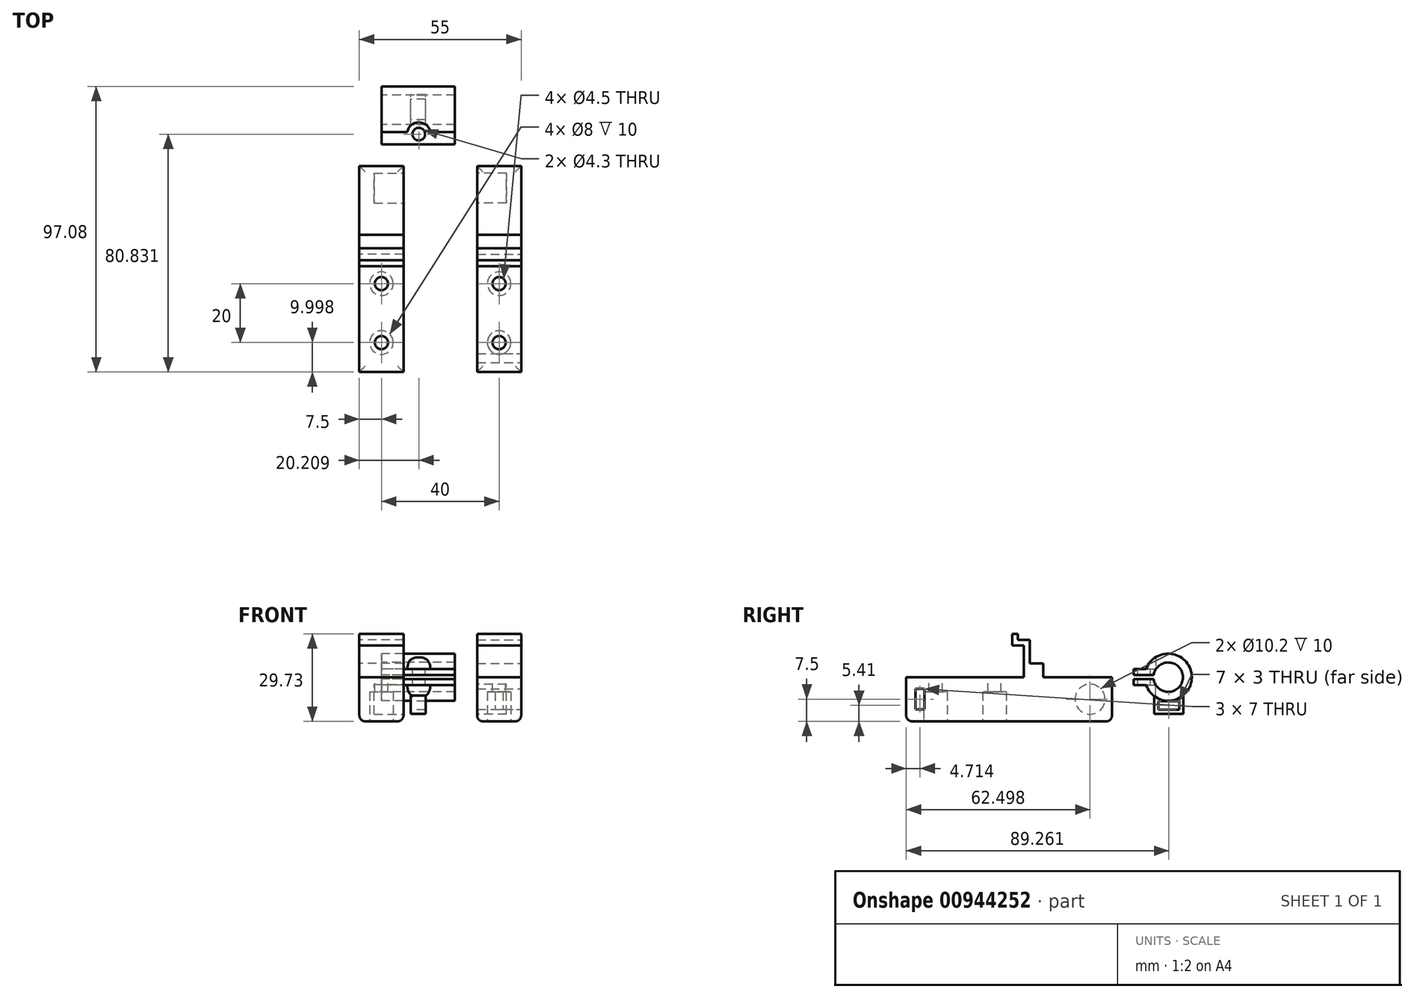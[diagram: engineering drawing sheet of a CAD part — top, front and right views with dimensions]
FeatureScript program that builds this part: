
annotation { "Feature Type Name" : "Feature", "Feature Type Description" : "" }
export const myFeature = defineFeature(function(context is Context, id is Id, definition is map)
    precondition{}
    {
        {
            var Q0;
            Q0=qCreatedBy(makeId("Top.planeOp"),FACE);
            var sketch = newSketch(context, id + "F0", { "sketchPlane" : qUnion([Q0])});
            skLineSegment(sketch, "E0", {"start": v(120.64, 20) * mm, "end": v(-98.83, 20) * mm, "construction": true});
            skLineSegment(sketch, "E1", {"start": v(-113.57, -20) * mm, "end": v(119.85, -20) * mm, "construction": true});
            skLineSegment(sketch, "E2", {"start": v(-15.81, 35.6) * mm, "end": v(120.22, 35.6) * mm, "construction": true});
            skLineSegment(sketch, "E3", {"start": v(0, 0) * mm, "end": v(121.2, 0) * mm, "construction": true});
            skSolve(sketch);
        }
        {
            var Q0;
            Q0=qCreatedBy(makeId("Right.planeOp"),FACE);
            var sketch = newSketch(context, id + "F1", { "sketchPlane" : qUnion([Q0])});
            skLineSegment(sketch, "E4", {"start": v(13.49, 0) * mm, "end": v(-26.51, 0) * mm});
            skLineSegment(sketch, "E5", {"start": v(-26.51, 0) * mm, "end": v(-26.51, -15) * mm});
            skLineSegment(sketch, "E6", {"start": v(-26.51, -15) * mm, "end": v(18.49, -15) * mm});
            skLineSegment(sketch, "E7", {"start": v(13.49, 10.73) * mm, "end": v(13.49, 0) * mm});
            skLineSegment(sketch, "E8", {"start": v(43.49, -15) * mm, "end": v(43.49, 0) * mm});
            skLineSegment(sketch, "E9", {"start": v(43.49, 0) * mm, "end": v(20.14, 0) * mm});
            skLineSegment(sketch, "E10", {"start": v(13.49, 10.73) * mm, "end": v(9.49, 10.73) * mm});
            skLineSegment(sketch, "E11", {"start": v(9.49, 10.73) * mm, "end": v(9.49, 14.73) * mm});
            skLineSegment(sketch, "E12", {"start": v(9.49, 14.73) * mm, "end": v(11.49, 14.73) * mm});
            skLineSegment(sketch, "E13", {"start": v(11.49, 14.73) * mm, "end": v(11.49, 12.73) * mm});
            skLineSegment(sketch, "E14", {"start": v(18.49, -15) * mm, "end": v(43.49, -15) * mm});
            skLineSegment(sketch, "E15", {"start": v(20.14, 0) * mm, "end": v(20.14, 4.7) * mm});
            skLineSegment(sketch, "E16", {"start": v(20.14, 4.7) * mm, "end": v(15.49, 4.7) * mm});
            skPoint(sketch, "E17.orphan", {"position": v(15.49, 0) * mm});
            skPoint(sketch, "E18.end.orphan", {"position": v(13.49, 21.47) * mm});
            skLineSegment(sketch, "E19", {"start": v(15.49, 4.7) * mm, "end": v(15.49, 12.7) * mm});
            skPoint(sketch, "E20.end.orphan", {"position": v(13.49, 12) * mm});
            skLineSegment(sketch, "E21", {"start": v(15.49, 12.7) * mm, "end": v(11.49, 12.73) * mm});
            skSolve(sketch);
        }
        {
            var Q0;
            Q0=makeQuery(id+"F1.imprint","IMPRINT",FACE,{"disambiguationData":[TD([[makeQuery(id+"F1.imprint","IMPRINT",EDGE,{"derivedFrom":sQuery(id+"F1.wireOp",EDGE,"E4")}),1.0]])]});
            var Q1;
            {var subQ0=sQuery(id+"F1.wireOp",EDGE,"E10");Q1=makeQuery(id+"F1.imprint","IMPRINT",FACE,{"disambiguationData":[TD([[makeQuery(id+"F1.imprint","IMPRINT",EDGE,{"derivedFrom":subQ0}),-1.0]])]});}
            extrude(context, id + "F2", {"entities" : qUnion([Q0, Q1]), "depth" : 15 * mm, "symmetric" : true});
        }
        {
            var Q0;
            Q0=makeQuery(id+"F2.opExtrude","CAP_FACE",FACE,{"disambiguationData":[OSD([sQuery(id+"F1.wireOp",EDGE,"E4"),sQuery(id+"F1.wireOp",EDGE,"E5"),sQuery(id+"F1.wireOp",EDGE,"E6"),sQuery(id+"F1.wireOp",EDGE,"E7"),sQuery(id+"F1.wireOp",EDGE,"E8"),sQuery(id+"F1.wireOp",EDGE,"E9"),sQuery(id+"F1.wireOp",EDGE,"E10"),sQuery(id+"F1.wireOp",EDGE,"E11"),sQuery(id+"F1.wireOp",EDGE,"E12"),sQuery(id+"F1.wireOp",EDGE,"E13"),sQuery(id+"F1.wireOp",EDGE,"E14"),sQuery(id+"F1.wireOp",EDGE,"E15"),sQuery(id+"F1.wireOp",EDGE,"E16"),sQuery(id+"F1.wireOp",EDGE,"E19"),sQuery(id+"F1.wireOp",EDGE,"E21")])],"isStart":false});
            var sketch = newSketch(context, id + "F3", { "sketchPlane" : qUnion([Q0])});
            skCircle(sketch, "E22", {"center": v(35.99, -7.5) * mm, "radius": 5.1 * mm});
            skSolve(sketch);
        }
        {
            var Q0;
            Q0=makeQuery(id+"F3.imprint","IMPRINT",FACE,{"disambiguationData":[TD([[makeQuery(id+"F3.imprint","IMPRINT",EDGE,{"derivedFrom":sQuery(id+"F3.wireOp",EDGE,"E22")}),1.0]])]});
            extrude(context, id + "F4", {"entities" : qUnion([Q0]), "operationType" : NewBodyOperationType.REMOVE, "oppositeDirection" : true, "depth" : 10 * mm});
        }
        {
            var Q0;
            Q0=qCreatedBy(makeId("Right.planeOp"),FACE);
            cPlane(context, id + "F5", {"entities" : qUnion([Q0]), "cplaneType" : CPlaneType.OFFSET, "offset" : 20 * mm, "width" : 150 * mm, "height" : 150 * mm});
        }
        {
            var Q0;
            Q0=makeQuery(id+"F2.opExtrude","SWEPT_BODY",BODY,{"disambiguationData":[OSD([sQuery(id+"F1.wireOp",EDGE,"E4"),sQuery(id+"F1.wireOp",EDGE,"E5"),sQuery(id+"F1.wireOp",EDGE,"E6"),sQuery(id+"F1.wireOp",EDGE,"E7"),sQuery(id+"F1.wireOp",EDGE,"E8"),sQuery(id+"F1.wireOp",EDGE,"E9"),sQuery(id+"F1.wireOp",EDGE,"E10"),sQuery(id+"F1.wireOp",EDGE,"E11"),sQuery(id+"F1.wireOp",EDGE,"E12"),sQuery(id+"F1.wireOp",EDGE,"E13"),sQuery(id+"F1.wireOp",EDGE,"E14"),sQuery(id+"F1.wireOp",EDGE,"E15"),sQuery(id+"F1.wireOp",EDGE,"E16"),sQuery(id+"F1.wireOp",EDGE,"E19"),sQuery(id+"F1.wireOp",EDGE,"E21")])]});
            var Q1;
            Q1=qCreatedBy(id+"F5.planeOp",FACE);
            mirror(context, id + "F6", {"entities" : qUnion([Q0]), "mirrorPlane" : qUnion([Q1])});
        }
        {
            var Q0;
            Q0=makeQuery(id+"F6.opPattern","COPY",FACE,{"derivedFrom":makeQuery(id+"F2.opExtrude","CAP_FACE",FACE,{"disambiguationData":[OSD([sQuery(id+"F1.wireOp",EDGE,"E4"),sQuery(id+"F1.wireOp",EDGE,"E5"),sQuery(id+"F1.wireOp",EDGE,"E6"),sQuery(id+"F1.wireOp",EDGE,"E7"),sQuery(id+"F1.wireOp",EDGE,"E8"),sQuery(id+"F1.wireOp",EDGE,"E9"),sQuery(id+"F1.wireOp",EDGE,"E10"),sQuery(id+"F1.wireOp",EDGE,"E11"),sQuery(id+"F1.wireOp",EDGE,"E12"),sQuery(id+"F1.wireOp",EDGE,"E13"),sQuery(id+"F1.wireOp",EDGE,"E14"),sQuery(id+"F1.wireOp",EDGE,"E15"),sQuery(id+"F1.wireOp",EDGE,"E16"),sQuery(id+"F1.wireOp",EDGE,"E19"),sQuery(id+"F1.wireOp",EDGE,"E21")])],"isStart":true}),"instanceName":"1"});
            var sketch = newSketch(context, id + "F7", { "sketchPlane" : qUnion([Q0])});
            skLineSegment(sketch, "E23.bottom", {"start": v(-20.3, -4) * mm, "end": v(-23.3, -4) * mm});
            skLineSegment(sketch, "E23.top", {"start": v(-20.3, -11) * mm, "end": v(-23.3, -11) * mm});
            skLineSegment(sketch, "E23.left", {"start": v(-20.3, -4) * mm, "end": v(-20.3, -11) * mm});
            skLineSegment(sketch, "E23.right", {"start": v(-23.3, -4) * mm, "end": v(-23.3, -11) * mm});
            skSolve(sketch);
        }
        {
            var Q0;
            Q0=makeQuery(id+"F7.imprint","IMPRINT",FACE,{"disambiguationData":[TD([[makeQuery(id+"F7.imprint","IMPRINT",EDGE,{"derivedFrom":sQuery(id+"F7.wireOp",EDGE,"E23.bottom")}),1.0]])]});
            extrude(context, id + "F8", {"entities" : qUnion([Q0]), "operationType" : NewBodyOperationType.REMOVE, "endBound" : BoundingType.UP_TO_NEXT, "oppositeDirection" : true, "depth" : 25 * mm});
        }
        {
            var Q0;
            Q0=makeQuery(id+"F8.boolean.opBoolean","COPY",EDGE,{"derivedFrom":makeQuery(id+"F8.opExtrude","CAP_EDGE",EDGE,{"disambiguationData":[OSD([sQuery(id+"F7.wireOp",EDGE,"E23.right")])],"isStart":true})});
            var Q1;
            Q1=makeQuery(id+"F8.boolean.opBoolean","COPY",EDGE,{"derivedFrom":makeQuery(id+"F8.opExtrude","TWEAK_EDGE",EDGE,{"derivedFrom":[makeQuery(id+"F6.opPattern","COPY",FACE,{"derivedFrom":makeQuery(id+"F2.opExtrude","CAP_FACE",FACE,{"disambiguationData":[OSD([sQuery(id+"F1.wireOp",EDGE,"E4"),sQuery(id+"F1.wireOp",EDGE,"E5"),sQuery(id+"F1.wireOp",EDGE,"E6"),sQuery(id+"F1.wireOp",EDGE,"E7"),sQuery(id+"F1.wireOp",EDGE,"E8"),sQuery(id+"F1.wireOp",EDGE,"E9"),sQuery(id+"F1.wireOp",EDGE,"E10"),sQuery(id+"F1.wireOp",EDGE,"E11"),sQuery(id+"F1.wireOp",EDGE,"E12"),sQuery(id+"F1.wireOp",EDGE,"E13"),sQuery(id+"F1.wireOp",EDGE,"E14"),sQuery(id+"F1.wireOp",EDGE,"E15"),sQuery(id+"F1.wireOp",EDGE,"E16"),sQuery(id+"F1.wireOp",EDGE,"E19"),sQuery(id+"F1.wireOp",EDGE,"E21")])],"isStart":false}),"instanceName":"1"}),makeQuery(id+"F7.imprint","IMPRINT",EDGE,{"derivedFrom":sQuery(id+"F7.wireOp",EDGE,"E23.right")})]})});
            var Q2;
            Q2=makeQuery(id+"F6.opPattern","COPY",EDGE,{"derivedFrom":makeQuery(id+"F2.opExtrude","CAP_EDGE",EDGE,{"disambiguationData":[OSD([sQuery(id+"F1.wireOp",EDGE,"E6"),sQuery(id+"F1.wireOp",EDGE,"E14")])],"isStart":false}),"instanceName":"1"});
            var Q3;
            Q3=makeQuery(id+"F6.opPattern","COPY",EDGE,{"derivedFrom":makeQuery(id+"F2.opExtrude","CAP_EDGE",EDGE,{"disambiguationData":[OSD([sQuery(id+"F1.wireOp",EDGE,"E6"),sQuery(id+"F1.wireOp",EDGE,"E14")])],"isStart":true}),"instanceName":"1"});
            var Q4;
            Q4=makeQuery(id+"F2.opExtrude","CAP_EDGE",EDGE,{"disambiguationData":[OSD([sQuery(id+"F1.wireOp",EDGE,"E6"),sQuery(id+"F1.wireOp",EDGE,"E14")])],"isStart":true});
            var Q5;
            Q5=makeQuery(id+"F2.opExtrude","CAP_EDGE",EDGE,{"disambiguationData":[OSD([sQuery(id+"F1.wireOp",EDGE,"E6"),sQuery(id+"F1.wireOp",EDGE,"E14")])],"isStart":false});
            var Q6;
            Q6=makeQuery(id+"F6.opPattern","COPY",EDGE,{"derivedFrom":makeQuery(id+"F2.opExtrude","SWEPT_EDGE",EDGE,{"disambiguationData":[OSD([sQuery(id+"F1.wireOp",EDGE,"E5"),sQuery(id+"F1.wireOp",EDGE,"E6")])]}),"instanceName":"1"});
            var Q7;
            Q7=makeQuery(id+"F2.opExtrude","SWEPT_EDGE",EDGE,{"disambiguationData":[OSD([sQuery(id+"F1.wireOp",EDGE,"E5"),sQuery(id+"F1.wireOp",EDGE,"E6")])]});
            var Q8;
            Q8=makeQuery(id+"F2.opExtrude","SWEPT_EDGE",EDGE,{"disambiguationData":[OSD([sQuery(id+"F1.wireOp",EDGE,"E8"),sQuery(id+"F1.wireOp",EDGE,"E14")])]});
            var Q9;
            Q9=makeQuery(id+"F6.opPattern","COPY",EDGE,{"derivedFrom":makeQuery(id+"F2.opExtrude","SWEPT_EDGE",EDGE,{"disambiguationData":[OSD([sQuery(id+"F1.wireOp",EDGE,"E8"),sQuery(id+"F1.wireOp",EDGE,"E14")])]}),"instanceName":"1"});
            fillet(context, id + "F9", {"entities" : qUnion([Q0, Q1, Q2, Q3, Q4, Q5, Q6, Q7, Q8, Q9]), "radius" : 2 * mm, "tangentPropagation" : true, "allowEdgeOverflow" : false});
        }
        {
            var Q0;
            Q0=makeQuery(id+"F2.opExtrude","SWEPT_FACE",FACE,{"disambiguationData":[OSD([sQuery(id+"F1.wireOp",EDGE,"E4")])]});
            var sketch = newSketch(context, id + "F10", { "sketchPlane" : qUnion([Q0])});
            skCircle(sketch, "E24", {"center": v(0, 3.49) * mm, "radius": 2.25 * mm});
            skCircle(sketch, "E25", {"center": v(0, -16.51) * mm, "radius": 2.25 * mm});
            skSolve(sketch);
        }
        {
            var Q0;
            Q0=makeQuery(id+"F10.imprint","IMPRINT",FACE,{"disambiguationData":[TD([[makeQuery(id+"F10.imprint","IMPRINT",EDGE,{"derivedFrom":sQuery(id+"F10.wireOp",EDGE,"E24")}),1.0]])]});
            var Q1;
            Q1=makeQuery(id+"F10.imprint","IMPRINT",FACE,{"disambiguationData":[TD([[makeQuery(id+"F10.imprint","IMPRINT",EDGE,{"derivedFrom":sQuery(id+"F10.wireOp",EDGE,"E25")}),1.0]])]});
            var Q2;
            Q2=sQuery(id+"F10.wireOp",EDGE,"E24");
            var Q3;
            Q3=sQuery(id+"F10.wireOp",EDGE,"E25");
            extrude(context, id + "F11", {"entities" : qUnion([Q0, Q1]), "operationType" : NewBodyOperationType.REMOVE, "surfaceEntities" : qUnion([Q2, Q3]), "endBound" : BoundingType.UP_TO_NEXT, "oppositeDirection" : true, "depth" : 25 * mm});
        }
        {
            var Q0;
            Q0=makeQuery(id+"F6.opPattern","COPY",FACE,{"derivedFrom":makeQuery(id+"F2.opExtrude","SWEPT_FACE",FACE,{"disambiguationData":[OSD([sQuery(id+"F1.wireOp",EDGE,"E4")])]}),"instanceName":"1"});
            var sketch = newSketch(context, id + "F12", { "sketchPlane" : qUnion([Q0])});
            skCircle(sketch, "E26", {"center": v(40, 3.49) * mm, "radius": 2.25 * mm});
            skCircle(sketch, "E27", {"center": v(40, -16.51) * mm, "radius": 2.25 * mm});
            skSolve(sketch);
        }
        {
            var Q0;
            Q0=makeQuery(id+"F12.imprint","IMPRINT",FACE,{"disambiguationData":[TD([[makeQuery(id+"F12.imprint","IMPRINT",EDGE,{"derivedFrom":sQuery(id+"F12.wireOp",EDGE,"E26")}),1.0]])]});
            var Q1;
            Q1=makeQuery(id+"F12.imprint","IMPRINT",FACE,{"disambiguationData":[TD([[makeQuery(id+"F12.imprint","IMPRINT",EDGE,{"derivedFrom":sQuery(id+"F12.wireOp",EDGE,"E27")}),1.0]])]});
            extrude(context, id + "F13", {"entities" : qUnion([Q0, Q1]), "operationType" : NewBodyOperationType.REMOVE, "endBound" : BoundingType.UP_TO_NEXT, "oppositeDirection" : true, "depth" : 25 * mm});
        }
        {
            var Q0;
            Q0=makeQuery(id+"F6.opPattern","COPY",FACE,{"derivedFrom":makeQuery(id+"F2.opExtrude","SWEPT_FACE",FACE,{"disambiguationData":[OSD([sQuery(id+"F1.wireOp",EDGE,"E6"),sQuery(id+"F1.wireOp",EDGE,"E14")])]}),"instanceName":"1"});
            var sketch = newSketch(context, id + "F14", { "sketchPlane" : qUnion([Q0])});
            skCircle(sketch, "E28", {"center": v(40, -3.49) * mm, "radius": 4 * mm});
            skCircle(sketch, "E29", {"center": v(40, 16.51) * mm, "radius": 4 * mm});
            skSolve(sketch);
        }
        {
            var Q0;
            Q0=makeQuery(id+"F14.imprint","IMPRINT",FACE,{"disambiguationData":[TD([[makeQuery(id+"F14.imprint","IMPRINT",EDGE,{"derivedFrom":sQuery(id+"F14.wireOp",EDGE,"E28")}),1.0]])]});
            var Q1;
            Q1=makeQuery(id+"F14.imprint","IMPRINT",FACE,{"disambiguationData":[TD([[makeQuery(id+"F14.imprint","IMPRINT",EDGE,{"derivedFrom":sQuery(id+"F14.wireOp",EDGE,"E29")}),1.0]])]});
            extrude(context, id + "F15", {"entities" : qUnion([Q0, Q1]), "operationType" : NewBodyOperationType.REMOVE, "oppositeDirection" : true, "depth" : 10 * mm});
        }
        {
            var Q0;
            Q0=makeQuery(id+"F2.opExtrude","SWEPT_FACE",FACE,{"disambiguationData":[OSD([sQuery(id+"F1.wireOp",EDGE,"E6"),sQuery(id+"F1.wireOp",EDGE,"E14")])]});
            var sketch = newSketch(context, id + "F16", { "sketchPlane" : qUnion([Q0])});
            skCircle(sketch, "E30", {"center": v(0, -3.49) * mm, "radius": 4 * mm});
            skCircle(sketch, "E31", {"center": v(0, 16.51) * mm, "radius": 4 * mm});
            skSolve(sketch);
        }
        {
            var Q0;
            Q0=makeQuery(id+"F16.imprint","IMPRINT",FACE,{"disambiguationData":[TD([[makeQuery(id+"F16.imprint","IMPRINT",EDGE,{"derivedFrom":sQuery(id+"F16.wireOp",EDGE,"E30")}),1.0]])]});
            var Q1;
            Q1=makeQuery(id+"F16.imprint","IMPRINT",FACE,{"disambiguationData":[TD([[makeQuery(id+"F16.imprint","IMPRINT",EDGE,{"derivedFrom":sQuery(id+"F16.wireOp",EDGE,"E31")}),1.0]])]});
            extrude(context, id + "F17", {"entities" : qUnion([Q0, Q1]), "operationType" : NewBodyOperationType.REMOVE, "oppositeDirection" : true, "depth" : 10 * mm});
        }
        {
            var Q0;
            Q0=qCreatedBy(makeId("Right.planeOp"),FACE);
            var sketch = newSketch(context, id + "F18", { "sketchPlane" : qUnion([Q0])});
            skArc(sketch, "E32", {"start": v(57.63, -0.71) * mm, "mid": v(67.57, 0) * mm, "end": v(57.63, 0.71) * mm});
            skArc(sketch, "E33", {"start": v(55.05, -2.71) * mm, "mid": v(70.57, 0) * mm, "end": v(55.05, 2.71) * mm});
            skLineSegment(sketch, "E34", {"start": v(57.63, -0.71) * mm, "end": v(54.6, -0.71) * mm});
            skLineSegment(sketch, "E35.MirrorCS", {"start": v(57.63, 0.71) * mm, "end": v(54.6, 0.71) * mm});
            skLineSegment(sketch, "E36.bottom", {"start": v(57.63, 0.71) * mm, "end": v(50.84, 0.71) * mm});
            skLineSegment(sketch, "E36.top", {"start": v(55.05, 2.71) * mm, "end": v(50.84, 2.71) * mm});
            skLineSegment(sketch, "E36.right", {"start": v(50.84, 0.71) * mm, "end": v(50.84, 2.71) * mm});
            skLineSegment(sketch, "E37.MirrorCS", {"start": v(55.05, -2.71) * mm, "end": v(50.84, -2.71) * mm});
            skLineSegment(sketch, "E38.MirrorCS", {"start": v(50.84, -0.71) * mm, "end": v(50.84, -2.71) * mm});
            skLineSegment(sketch, "E39.MirrorCS", {"start": v(57.63, -0.71) * mm, "end": v(50.84, -0.71) * mm});
            skPoint(sketch, "E40.orphan", {"position": v(57.63, -2.71) * mm});
            skPoint(sketch, "E41.MirrorCS.start.orphan", {"position": v(57.63, -0.71) * mm});
            skPoint(sketch, "E36.left.end.orphan", {"position": v(57.63, 2.71) * mm});
            skSolve(sketch);
        }
        {
            var Q0;
            {var subQ3=sQuery(id+"F18.wireOp",EDGE,"E32");Q0=makeQuery(id+"F18.imprint","IMPRINT",FACE,{"disambiguationData":[TD([[makeQuery(id+"F18.imprint","IMPRINT",EDGE,{"derivedFrom":subQ3}),-1.0]])]});}
            extrude(context, id + "F19", {"entities" : qUnion([Q0]), "depth" : 25 * mm});
        }
        {
            var Q0;
            Q0=qCreatedBy(makeId("Top.planeOp"),FACE);
            var sketch = newSketch(context, id + "F20", { "sketchPlane" : qUnion([Q0])});
            skCircle(sketch, "E42", {"center": v(12.7, 54.32) * mm, "radius": 2.15 * mm});
            skSolve(sketch);
        }
        {
            var Q0;
            Q0=qSketchRegion(id+"F20",true);
            var Q1;
            Q1=sQuery(id+"F20.wireOp",EDGE,"E42");
            extrude(context, id + "F21", {"entities" : qUnion([Q0]), "operationType" : NewBodyOperationType.REMOVE, "surfaceEntities" : qUnion([Q1]), "oppositeDirection" : true, "depth" : 25 * mm, "symmetric" : true});
        }
        {
            var Q0;
            Q0=makeQuery(id+"F19.opExtrude","SWEPT_FACE",FACE,{"disambiguationData":[OSD([sQuery(id+"F18.wireOp",EDGE,"E37.MirrorCS")])]});
            var sketch = newSketch(context, id + "F22", { "sketchPlane" : qUnion([Q0])});
            skCircle(sketch, "E43", {"center": v(12.7, -54.32) * mm, "radius": 4 * mm});
            skSolve(sketch);
        }
        {
            var Q0;
            Q0=qSketchRegion(id+"F22",true);
            extrude(context, id + "F23", {"entities" : qUnion([Q0]), "operationType" : NewBodyOperationType.REMOVE, "depth" : 25 * mm});
        }
        {
            var Q0;
            Q0=makeQuery(id+"F19.opExtrude","SWEPT_FACE",FACE,{"disambiguationData":[OSD([sQuery(id+"F18.wireOp",EDGE,"E36.top")])]});
            var sketch = newSketch(context, id + "F24", { "sketchPlane" : qUnion([Q0])});
            skCircle(sketch, "E44", {"center": v(12.7, 54.32) * mm, "radius": 4 * mm});
            skSolve(sketch);
        }
        {
            var Q0;
            Q0=qSketchRegion(id+"F24",true);
            extrude(context, id + "F25", {"entities" : qUnion([Q0]), "operationType" : NewBodyOperationType.REMOVE, "depth" : 25 * mm});
        }
        {
            var Q0;
            Q0=qCreatedBy(makeId("Right.planeOp"),FACE);
            cPlane(context, id + "F26", {"entities" : qUnion([Q0]), "cplaneType" : CPlaneType.OFFSET, "offset" : 12.5 * mm, "width" : 150 * mm, "height" : 150 * mm});
        }
        {
            var Q0;
            Q0=qCreatedBy(id+"F26.planeOp",FACE);
            var sketch = newSketch(context, id + "F27", { "sketchPlane" : qUnion([Q0])});
            skLineSegment(sketch, "E45.bottom", {"start": v(57.76, -6.3) * mm, "end": v(57.75, -12.5) * mm});
            skLineSegment(sketch, "E45.left", {"start": v(57.76, -6.3) * mm, "end": v(62.76, -6.3) * mm});
            skLineSegment(sketch, "E46.MirrorCS", {"start": v(67.76, -6.3) * mm, "end": v(67.76, -12.5) * mm});
            skLineSegment(sketch, "E47.MirrorCS", {"start": v(67.76, -6.3) * mm, "end": v(62.76, -6.3) * mm});
            skLineSegment(sketch, "E48", {"start": v(57.75, -12.5) * mm, "end": v(67.76, -12.5) * mm});
            skLineSegment(sketch, "E49.bottom", {"start": v(59.25, -11.09) * mm, "end": v(59.25, -8.09) * mm});
            skLineSegment(sketch, "E49.top", {"start": v(66.25, -11.09) * mm, "end": v(66.25, -8.09) * mm});
            skLineSegment(sketch, "E49.left", {"start": v(59.25, -11.09) * mm, "end": v(66.25, -11.09) * mm});
            skLineSegment(sketch, "E49.right", {"start": v(59.25, -8.09) * mm, "end": v(66.25, -8.09) * mm});
            skSolve(sketch);
        }
        {
            var Q0;
            Q0=qSketchRegion(id+"F27",true);
            extrude(context, id + "F28", {"entities" : qUnion([Q0]), "operationType" : NewBodyOperationType.ADD, "depth" : 5 * mm, "symmetric" : true});
        }
    });
